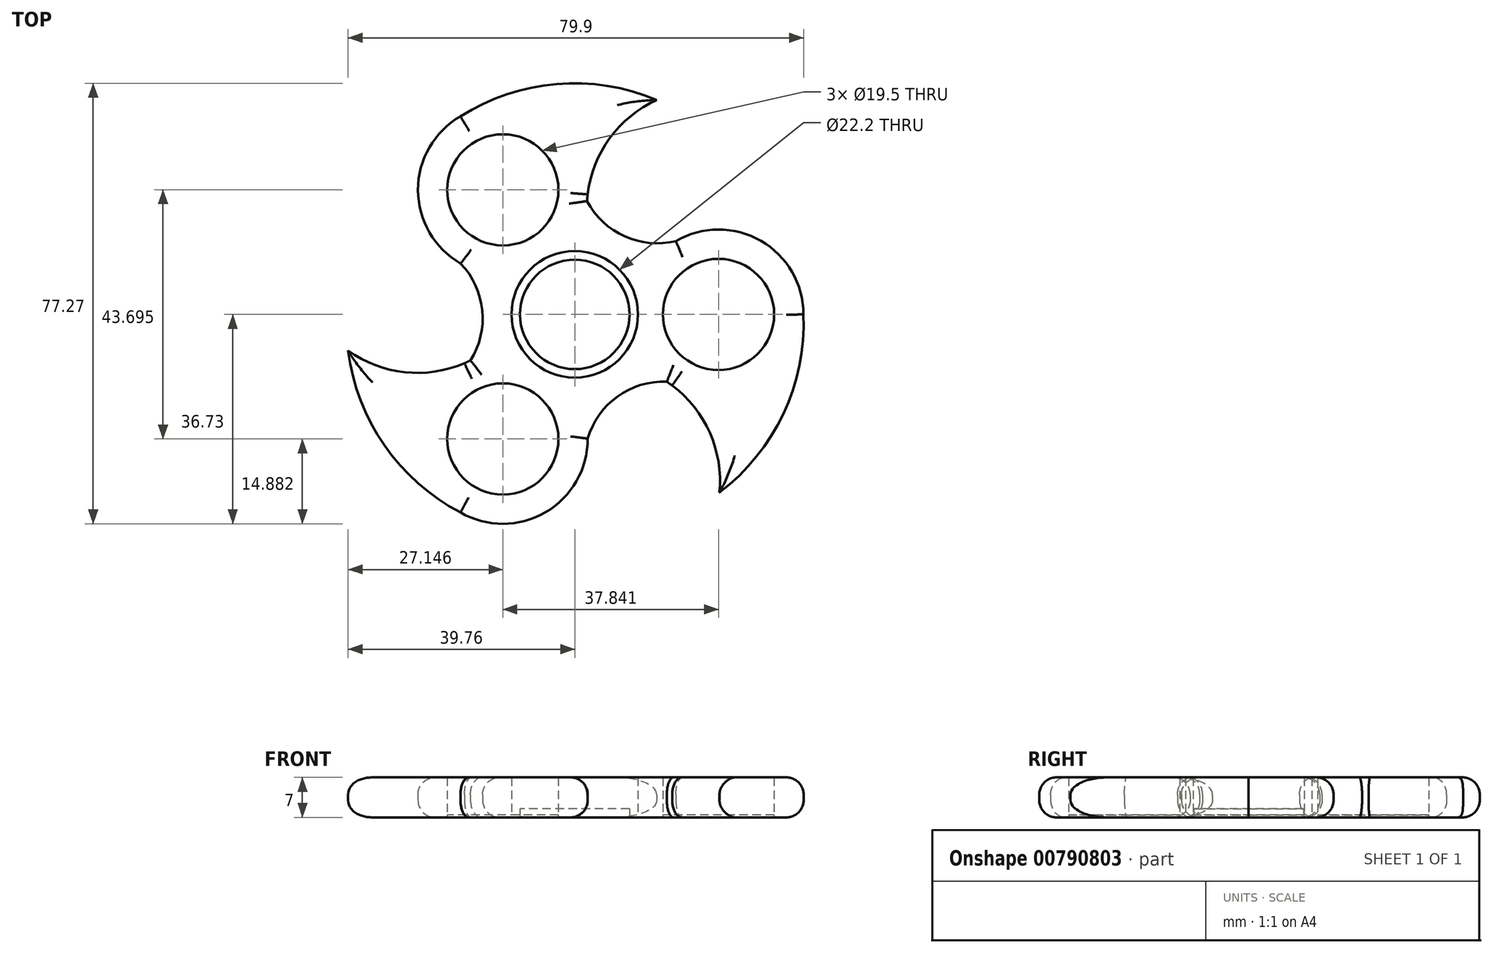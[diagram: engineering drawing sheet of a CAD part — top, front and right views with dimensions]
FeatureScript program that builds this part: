
annotation { "Feature Type Name" : "Feature", "Feature Type Description" : "" }
export const myFeature = defineFeature(function(context is Context, id is Id, definition is map)
    precondition{}
    {
        {
            var Q0;
            Q0=qCreatedBy(makeId("Top.planeOp"),FACE);
            var sketch = newSketch(context, id + "F0", { "sketchPlane" : qUnion([Q0])});
            skCircle(sketch, "E0", {"center": v(0, 0) * mm, "radius": 11.1 * mm});
            skCircle(sketch, "E1", {"center": v(25.23, 0) * mm, "radius": 9.75 * mm});
            skCircle(sketch, "E2.1.0", {"center": v(-12.61, 21.85) * mm, "radius": 9.75 * mm});
            skCircle(sketch, "E2.2.0", {"center": v(-12.61, -21.85) * mm, "radius": 9.75 * mm});
            skArc(sketch, "E3.0", {"start": v(-18.3, -8.1) * mm, "mid": v(-18.83, -8.32) * mm, "end": v(-19.35, -8.57) * mm});
            skArc(sketch, "E4.0", {"start": v(16.16, -11.8) * mm, "mid": v(16.62, -12.15) * mm, "end": v(17.1, -12.47) * mm});
            skArc(sketch, "E5", {"start": v(25.39, -31.25) * mm, "mid": v(36.59, -17.44) * mm, "end": v(40.11, 0) * mm});
            skArc(sketch, "E6", {"start": v(25.39, -31.25) * mm, "mid": v(23.46, -20.25) * mm, "end": v(16.16, -11.8) * mm});
            skArc(sketch, "E7.1.0", {"start": v(14.37, 37.61) * mm, "mid": v(5.81, 30.44) * mm, "end": v(2.14, 19.9) * mm});
            skArc(sketch, "E7.1.1", {"start": v(14.37, 37.61) * mm, "mid": v(-3.2, 40.4) * mm, "end": v(-20.06, 34.74) * mm});
            skArc(sketch, "E7.2.0", {"start": v(-39.76, -6.36) * mm, "mid": v(-29.27, -10.19) * mm, "end": v(-18.3, -8.1) * mm});
            skArc(sketch, "E7.2.1", {"start": v(-39.76, -6.36) * mm, "mid": v(-33.4, -22.97) * mm, "end": v(-20.06, -34.74) * mm});
            skArc(sketch, "E8", {"start": v(16.16, -11.8) * mm, "mid": v(7.5, -14.41) * mm, "end": v(2.27, -21.8) * mm});
            skArc(sketch, "E9.1.0", {"start": v(2.14, 19.9) * mm, "mid": v(8.73, 13.7) * mm, "end": v(17.74, 12.86) * mm});
            skArc(sketch, "E9.2.0", {"start": v(-18.3, -8.1) * mm, "mid": v(-16.23, 0.71) * mm, "end": v(-20.01, 8.93) * mm});
            skArc(sketch, "E10.trimOffspring", {"start": v(2.14, 19.9) * mm, "mid": v(2.2, 20.47) * mm, "end": v(2.25, 21.04) * mm});
            skArc(sketch, "E11.trimOffspring", {"start": v(40.11, 0) * mm, "mid": v(32.65, 12.9) * mm, "end": v(17.74, 12.86) * mm});
            skArc(sketch, "E12.trimOffspring", {"start": v(-20.06, -34.74) * mm, "mid": v(-5.15, -34.72) * mm, "end": v(2.27, -21.8) * mm});
            skArc(sketch, "E13.trimOffspring", {"start": v(-20.06, 34.74) * mm, "mid": v(-27.5, 21.82) * mm, "end": v(-20.01, 8.93) * mm});
            skSolve(sketch);
        }
        {
            var Q0;
            Q0=makeQuery(id+"F0.imprint","IMPRINT",FACE,{"disambiguationData":[TD([[makeQuery(id+"F0.imprint","IMPRINT",EDGE,{"derivedFrom":sQuery(id+"F0.wireOp",EDGE,"E2.1.0")}),1.0]])]});
            var Q1;
            Q1=makeQuery(id+"F0.imprint","IMPRINT",FACE,{"disambiguationData":[TD([[makeQuery(id+"F0.imprint","IMPRINT",EDGE,{"derivedFrom":sQuery(id+"F0.wireOp",EDGE,"E1")}),1.0]])]});
            var Q2;
            Q2=makeQuery(id+"F0.imprint","IMPRINT",FACE,{"disambiguationData":[TD([[makeQuery(id+"F0.imprint","IMPRINT",EDGE,{"derivedFrom":sQuery(id+"F0.wireOp",EDGE,"E2.2.0")}),1.0]])]});
            extrude(context, id + "F1", {"entities" : qUnion([Q0, Q1, Q2]), "depth" : 0.4 * mm, "offsetDistance" : 25 * mm});
        }
        {
            var Q0;
            Q0 = qSketchRegion(id + "F0", true);
            extrude(context, id + "F2", {"entities" : qUnion([Q0]), "depth" : 7 * mm, "offsetDistance" : 25 * mm});
        }
        {
            var Q0;
            Q0=makeQuery(id+"F2.opExtrude","CAP_EDGE",EDGE,{"disambiguationData":[OSD([sQuery(id+"F0.wireOp",EDGE,"E5")])],"isStart":false});
            var Q1;
            Q1=makeQuery(id+"F2.opExtrude","CAP_EDGE",EDGE,{"disambiguationData":[OSD([sQuery(id+"F0.wireOp",EDGE,"E9.1.0")])],"isStart":false});
            var Q2;
            Q2=makeQuery(id+"F2.opExtrude","CAP_EDGE",EDGE,{"disambiguationData":[OSD([sQuery(id+"F0.wireOp",EDGE,"E11.trimOffspring")])],"isStart":false});
            var Q3;
            Q3=makeQuery(id+"F2.opExtrude","CAP_EDGE",EDGE,{"disambiguationData":[OSD([sQuery(id+"F0.wireOp",EDGE,"E6")])],"isStart":false});
            var Q4;
            Q4=makeQuery(id+"F2.opExtrude","CAP_EDGE",EDGE,{"disambiguationData":[OSD([sQuery(id+"F0.wireOp",EDGE,"E8")])],"isStart":false});
            var Q5;
            Q5=makeQuery(id+"F2.opExtrude","CAP_EDGE",EDGE,{"disambiguationData":[OSD([sQuery(id+"F0.wireOp",EDGE,"E4.0")])],"isStart":false});
            var Q6;
            Q6=makeQuery(id+"F2.opExtrude","CAP_EDGE",EDGE,{"disambiguationData":[OSD([sQuery(id+"F0.wireOp",EDGE,"E12.trimOffspring")])],"isStart":false});
            var Q7;
            Q7=makeQuery(id+"F2.opExtrude","CAP_EDGE",EDGE,{"disambiguationData":[OSD([sQuery(id+"F0.wireOp",EDGE,"E7.1.0")])],"isStart":false});
            var Q8;
            Q8=makeQuery(id+"F2.opExtrude","CAP_EDGE",EDGE,{"disambiguationData":[OSD([sQuery(id+"F0.wireOp",EDGE,"E7.1.1")])],"isStart":false});
            var Q9;
            Q9=makeQuery(id+"F2.opExtrude","CAP_EDGE",EDGE,{"disambiguationData":[OSD([sQuery(id+"F0.wireOp",EDGE,"E13.trimOffspring")])],"isStart":false});
            var Q10;
            Q10=makeQuery(id+"F2.opExtrude","CAP_EDGE",EDGE,{"disambiguationData":[OSD([sQuery(id+"F0.wireOp",EDGE,"E9.2.0")])],"isStart":false});
            var Q11;
            Q11=makeQuery(id+"F2.opExtrude","CAP_EDGE",EDGE,{"disambiguationData":[OSD([sQuery(id+"F0.wireOp",EDGE,"E7.2.0")])],"isStart":false});
            var Q12;
            Q12=makeQuery(id+"F2.opExtrude","CAP_EDGE",EDGE,{"disambiguationData":[OSD([sQuery(id+"F0.wireOp",EDGE,"E3.0")])],"isStart":false});
            var Q13;
            Q13=makeQuery(id+"F2.opExtrude","CAP_EDGE",EDGE,{"disambiguationData":[OSD([sQuery(id+"F0.wireOp",EDGE,"E10.trimOffspring")])],"isStart":false});
            var Q14;
            Q14=makeQuery(id+"F2.opExtrude","CAP_EDGE",EDGE,{"disambiguationData":[OSD([sQuery(id+"F0.wireOp",EDGE,"E7.1.1")])],"isStart":true});
            var Q15;
            Q15=makeQuery(id+"F2.opExtrude","CAP_EDGE",EDGE,{"disambiguationData":[OSD([sQuery(id+"F0.wireOp",EDGE,"E7.1.0")])],"isStart":true});
            var Q16;
            Q16=makeQuery(id+"F2.opExtrude","CAP_EDGE",EDGE,{"disambiguationData":[OSD([sQuery(id+"F0.wireOp",EDGE,"E13.trimOffspring")])],"isStart":true});
            var Q17;
            Q17=makeQuery(id+"F2.opExtrude","CAP_EDGE",EDGE,{"disambiguationData":[OSD([sQuery(id+"F0.wireOp",EDGE,"E9.2.0")])],"isStart":true});
            var Q18;
            Q18=makeQuery(id+"F2.opExtrude","CAP_EDGE",EDGE,{"disambiguationData":[OSD([sQuery(id+"F0.wireOp",EDGE,"E7.2.0")])],"isStart":true});
            var Q19;
            Q19=makeQuery(id+"F2.opExtrude","CAP_EDGE",EDGE,{"disambiguationData":[OSD([sQuery(id+"F0.wireOp",EDGE,"E3.0")])],"isStart":true});
            var Q20;
            Q20=makeQuery(id+"F2.opExtrude","CAP_EDGE",EDGE,{"disambiguationData":[OSD([sQuery(id+"F0.wireOp",EDGE,"E12.trimOffspring")])],"isStart":true});
            var Q21;
            Q21=makeQuery(id+"F2.opExtrude","CAP_EDGE",EDGE,{"disambiguationData":[OSD([sQuery(id+"F0.wireOp",EDGE,"E7.2.1")])],"isStart":true});
            var Q22;
            Q22=makeQuery(id+"F2.opExtrude","CAP_EDGE",EDGE,{"disambiguationData":[OSD([sQuery(id+"F0.wireOp",EDGE,"E8")])],"isStart":true});
            var Q23;
            Q23=makeQuery(id+"F2.opExtrude","CAP_EDGE",EDGE,{"disambiguationData":[OSD([sQuery(id+"F0.wireOp",EDGE,"E4.0")])],"isStart":true});
            var Q24;
            Q24=makeQuery(id+"F2.opExtrude","CAP_EDGE",EDGE,{"disambiguationData":[OSD([sQuery(id+"F0.wireOp",EDGE,"E5")])],"isStart":true});
            var Q25;
            Q25=makeQuery(id+"F2.opExtrude","CAP_EDGE",EDGE,{"disambiguationData":[OSD([sQuery(id+"F0.wireOp",EDGE,"E11.trimOffspring")])],"isStart":true});
            var Q26;
            Q26=makeQuery(id+"F2.opExtrude","CAP_EDGE",EDGE,{"disambiguationData":[OSD([sQuery(id+"F0.wireOp",EDGE,"E9.1.0")])],"isStart":true});
            var Q27;
            Q27=makeQuery(id+"F2.opExtrude","CAP_EDGE",EDGE,{"disambiguationData":[OSD([sQuery(id+"F0.wireOp",EDGE,"E10.trimOffspring")])],"isStart":true});
            fillet(context, id + "F3", {"entities" : qUnion([Q0, Q1, Q2, Q3, Q4, Q5, Q6, Q7, Q8, Q9, Q10, Q11, Q12, Q13, Q14, Q15, Q16, Q17, Q18, Q19, Q20, Q21, Q22, Q23, Q24, Q25, Q26, Q27]), "radius" : 3 * mm, "tangentPropagation" : true, "allowEdgeOverflow" : false});
        }
        {
            var Q0;
            Q0=qCreatedBy(makeId("Top.planeOp"),FACE);
            var sketch = newSketch(context, id + "F4", { "sketchPlane" : qUnion([Q0])});
            skCircle(sketch, "E14", {"center": v(0, 0) * mm, "radius": 9.6 * mm});
            skSolve(sketch);
        }
        {
            var Q0;
            Q0 = qSketchRegion(id + "F4", true);
            extrude(context, id + "F5", {"entities" : qUnion([Q0]), "depth" : 1.5 * mm, "offsetDistance" : 25 * mm});
        }
    });
